# Revit family: DuraCare-Dining_Chair-Jefferson-
name_source: partatom
category: Furniture
revit_build: Autodesk Revit 2016 (Build: 20150220_1215(x64)
units: mm (PartAtom-declared; Revit-internal decimal feet)

## family parameters
Always vertical = Yes
Cut with Voids When Loaded = No
OmniClass Number = 23.40.20.00
OmniClass Title = General Furniture and Specialties
Room Calculation Point = No
Shared = No
Work Plane-Based = No

## types (1)
- AC-425
    Arm Height = 26"
    Assembly Code = E2020200
    Boot Finish = DUR - Plastic Boot
    Depth = 26 1/2"
    Description = Dining Chair 23.5"W x 26.5"D x 38.25"H - aluminum frame - wood grain finish
    Height = 38 1/2"
    Keynote = 12500
    Low Emitting Finish = Yes
    Low Emitting Material = Yes
    Manufacturer = DuraCare Seating
    Model = AC-425
    Percentage of Recycled Content = 0
    Product Documentation Link = https://duracareseating.com
    Revit Model Built By = https://servex-us.com
    Salvage or Reuse = Yes
    Seat height = 19 1/4"
    Type Comments = Jefferson
    URL = https://duracareseating.com
    Wheel Finish = DUR - Plastic Black
    Width = 23 1/2"

## geometry (parser evidence)
native form markers: Sweep x5
no freeform markers — native parametric forms only
